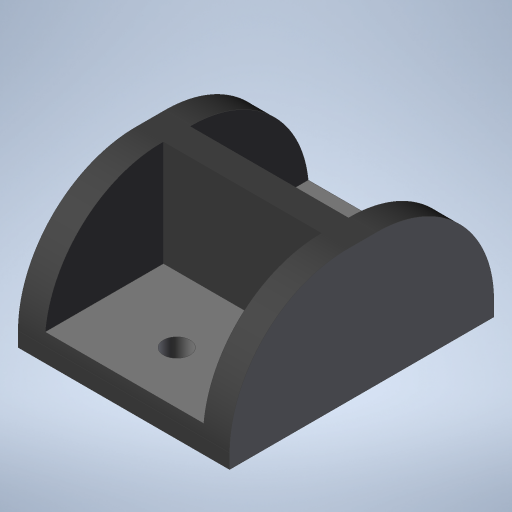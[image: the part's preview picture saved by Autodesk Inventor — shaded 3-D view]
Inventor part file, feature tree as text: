
AUTODESK INVENTOR PART (.ipt)
format: ipt  version: 2023 (Build 270158000, 158)  size: 250,368 bytes
history: native  units: mm
features: extrude x2, sketch x2, fillet x1
ambient origin geometry x8: Origin, YZ Plane, XZ Plane, XY Plane, X Axis, Y Axis, Z Axis, Center Point
bodies: Solid1 (feature_tree)
feature tree (5):
  extrude  "Extrusion1"  Depth=50.0mm
  extrude  "Extrusion2"  Depth=5.0mm
  fillet  "Fillet1"  Radius=10.0mm
  sketch  "Sketch1"  dims[d0=40.0mm d1=50.0mm]
  sketch  "Sketch2"  dims[d2=5.0mm d3=5.0mm d4=10.0mm d5=10.0mm d6=20.0mm d7=5.0mm d8=0.0mm d9=5.0mm d10=22.5mm d11=20.0mm d12=0.0mm d13=5.0mm d14=5.0mm d15=22.25mm]
